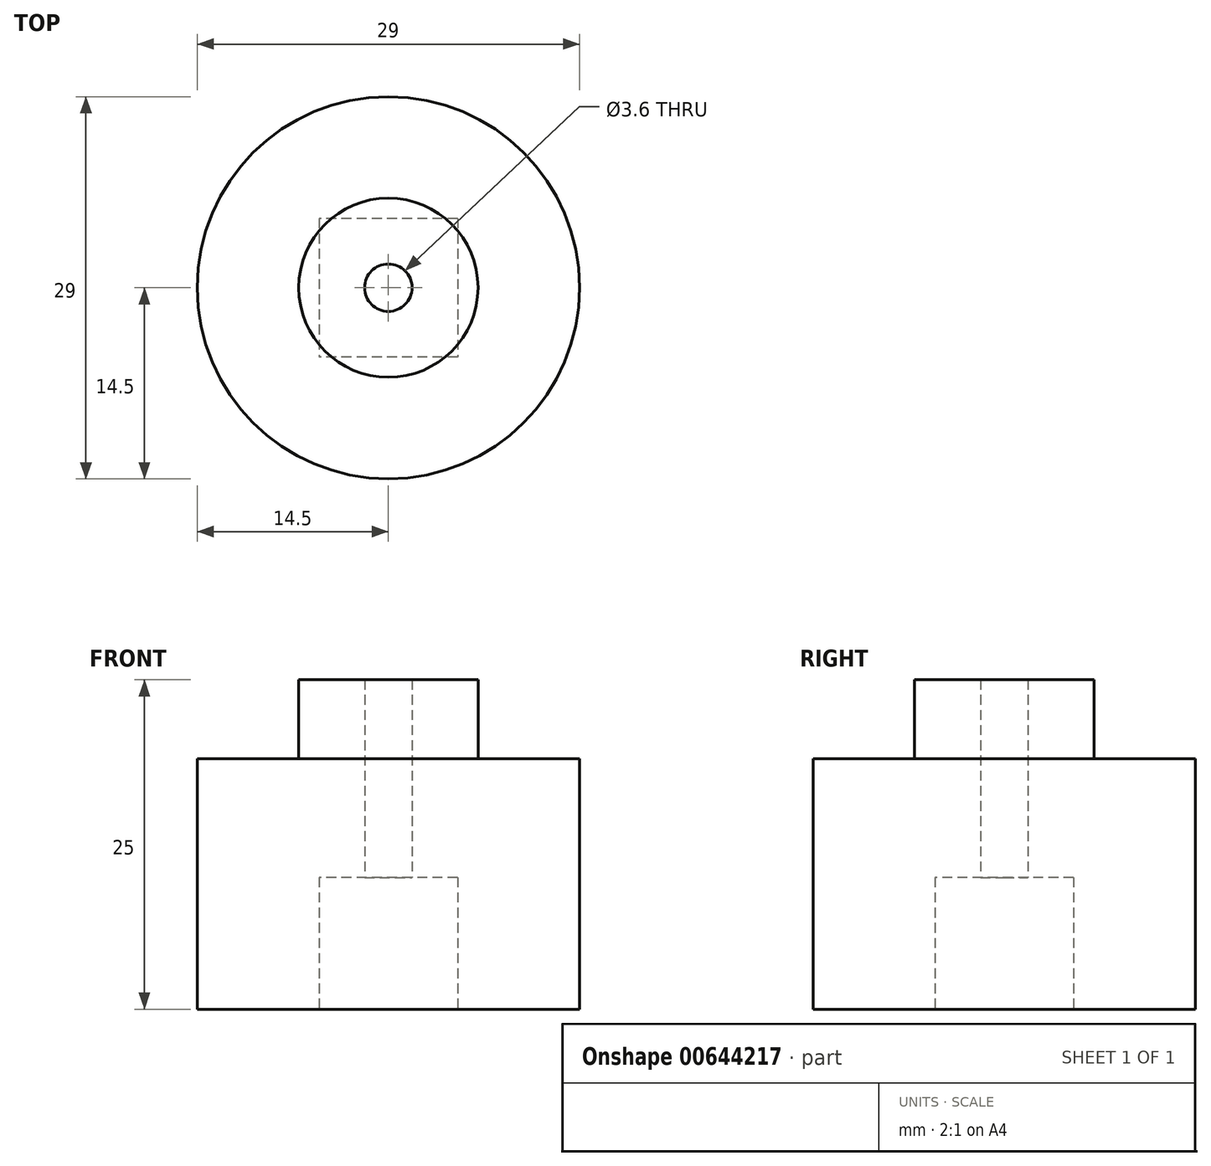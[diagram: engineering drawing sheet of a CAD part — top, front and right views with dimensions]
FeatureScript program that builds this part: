
annotation { "Feature Type Name" : "Feature", "Feature Type Description" : "" }
export const myFeature = defineFeature(function(context is Context, id is Id, definition is map)
    precondition{}
    {
        {
            var Q0;
            Q0=qCreatedBy(makeId("Top.planeOp"),FACE);
            var sketch = newSketch(context, id + "F0", { "sketchPlane" : qUnion([Q0])});
            skCircle(sketch, "E0", {"center": v(0, 0) * mm, "radius": 14.5 * mm});
            skSolve(sketch);
        }
        {
            var Q0;
            Q0=makeQuery(id+"F0.imprint","IMPRINT",FACE,{"disambiguationData":[TD([[makeQuery(id+"F0.imprint","IMPRINT",EDGE,{"derivedFrom":sQuery(id+"F0.wireOp",EDGE,"E0")}),1.0]])]});
            extrude(context, id + "F1", {"entities" : qUnion([Q0]), "depth" : 19 * mm, "offsetDistance" : 25 * mm});
        }
        {
            var Q0;
            Q0=makeQuery(id+"F1.opExtrude","CAP_FACE",FACE,{"disambiguationData":[OSD([sQuery(id+"F0.wireOp",EDGE,"E0")])],"isStart":false});
            var sketch = newSketch(context, id + "F2", { "sketchPlane" : qUnion([Q0])});
            skCircle(sketch, "E1", {"center": v(0, 0) * mm, "radius": 6.8 * mm});
            skSolve(sketch);
        }
        {
            var Q0;
            Q0=makeQuery(id+"F2.imprint","IMPRINT",FACE,{"disambiguationData":[TD([[makeQuery(id+"F2.imprint","IMPRINT",EDGE,{"derivedFrom":sQuery(id+"F2.wireOp",EDGE,"E1")}),1.0]])]});
            extrude(context, id + "F3", {"entities" : qUnion([Q0]), "operationType" : NewBodyOperationType.ADD, "depth" : 6 * mm, "offsetDistance" : 25 * mm});
        }
        {
            var Q0;
            Q0=makeQuery(id+"F1.opExtrude","CAP_FACE",FACE,{"disambiguationData":[OSD([sQuery(id+"F0.wireOp",EDGE,"E0")])],"isStart":true});
            var sketch = newSketch(context, id + "F4", { "sketchPlane" : qUnion([Q0])});
            skLineSegment(sketch, "E2.bottom", {"start": v(5.25, -5.25) * mm, "end": v(-5.25, -5.25) * mm});
            skLineSegment(sketch, "E2.top", {"start": v(5.25, 5.25) * mm, "end": v(-5.25, 5.25) * mm});
            skLineSegment(sketch, "E2.left", {"start": v(5.25, -5.25) * mm, "end": v(5.25, 5.25) * mm});
            skLineSegment(sketch, "E2.right", {"start": v(-5.25, -5.25) * mm, "end": v(-5.25, 5.25) * mm});
            skPoint(sketch, "E2.middle", {"position": v(0, 0) * mm});
            skSolve(sketch);
        }
        {
            var Q0;
            Q0=makeQuery(id+"F4.imprint","IMPRINT",FACE,{"disambiguationData":[TD([[makeQuery(id+"F4.imprint","IMPRINT",EDGE,{"derivedFrom":sQuery(id+"F4.wireOp",EDGE,"E2.bottom")}),-1.0]])]});
            extrude(context, id + "F5", {"entities" : qUnion([Q0]), "operationType" : NewBodyOperationType.REMOVE, "oppositeDirection" : true, "depth" : 10 * mm, "offsetDistance" : 25 * mm});
        }
        {
            var Q0;
            Q0=makeQuery(id+"F5.boolean.opBoolean","COPY",FACE,{"derivedFrom":makeQuery(id+"F5.opExtrude","CAP_FACE",FACE,{"disambiguationData":[OSD([sQuery(id+"F4.wireOp",EDGE,"E2.bottom"),sQuery(id+"F4.wireOp",EDGE,"E2.top"),sQuery(id+"F4.wireOp",EDGE,"E2.left"),sQuery(id+"F4.wireOp",EDGE,"E2.right")])],"isStart":false})});
            var sketch = newSketch(context, id + "F6", { "sketchPlane" : qUnion([Q0])});
            skCircle(sketch, "E3", {"center": v(0, 0) * mm, "radius": 1.8 * mm});
            skSolve(sketch);
        }
        {
            var Q0;
            Q0=makeQuery(id+"F6.imprint","IMPRINT",FACE,{"disambiguationData":[TD([[makeQuery(id+"F6.imprint","IMPRINT",EDGE,{"derivedFrom":sQuery(id+"F6.wireOp",EDGE,"E3")}),1.0]])]});
            extrude(context, id + "F7", {"entities" : qUnion([Q0]), "operationType" : NewBodyOperationType.REMOVE, "oppositeDirection" : true, "depth" : 25 * mm, "offsetDistance" : 25 * mm});
        }
    });
